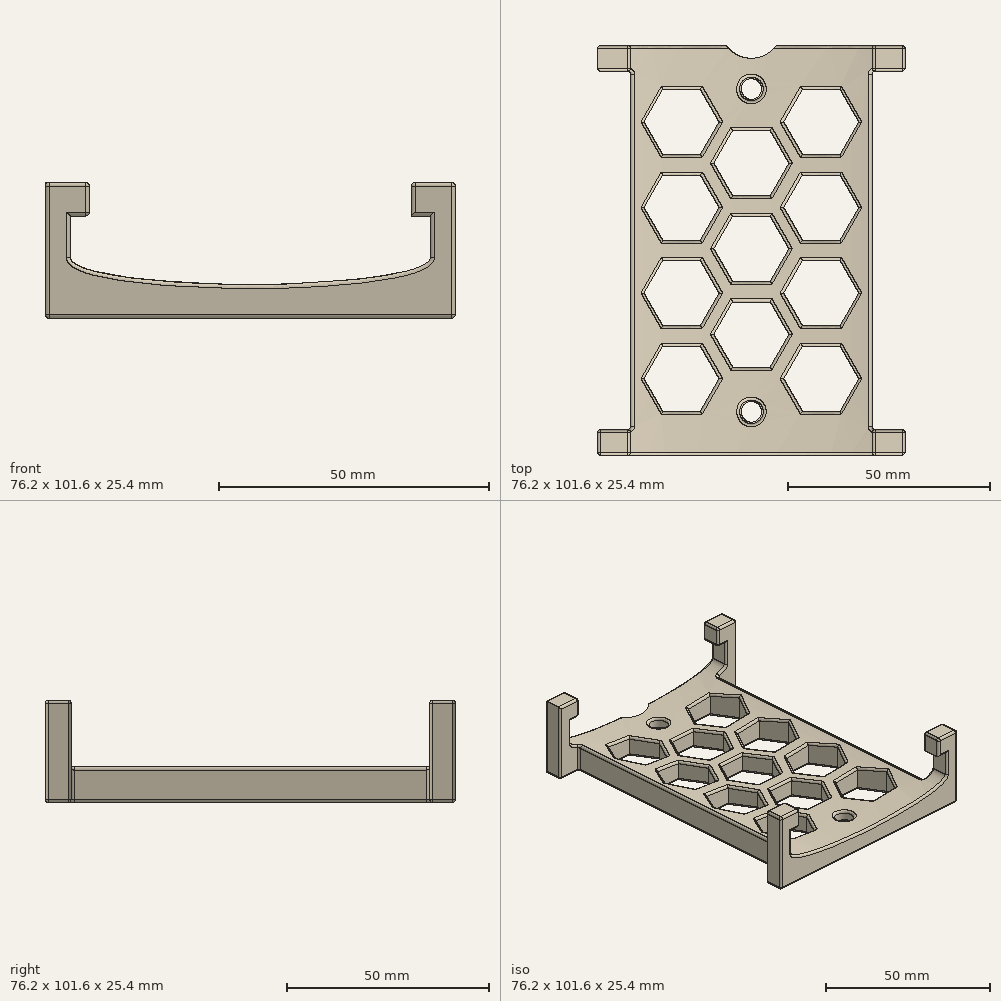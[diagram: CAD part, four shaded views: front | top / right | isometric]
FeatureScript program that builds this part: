
annotation { "Feature Type Name" : "Feature", "Feature Type Description" : "" }
export const myFeature = defineFeature(function(context is Context, id is Id, definition is map)
    precondition{}
    {
        {
            var Q0;
            Q0=qCreatedBy(makeId("Front.planeOp"),FACE);
            var sketch = newSketch(context, id + "F0", { "sketchPlane" : qUnion([Q0])});
            skLineSegment(sketch, "E0.bottom", {"start": v(-38.1, 25.4) * mm, "end": v(38.1, 25.4) * mm});
            skLineSegment(sketch, "E0.top", {"start": v(-38.1, 0) * mm, "end": v(38.1, 0) * mm});
            skLineSegment(sketch, "E0.left", {"start": v(-38.1, 25.4) * mm, "end": v(-38.1, 0) * mm});
            skLineSegment(sketch, "E0.right", {"start": v(38.1, 25.4) * mm, "end": v(38.1, 0) * mm});
            skLineSegment(sketch, "E1.top", {"start": v(33.46, 19.05) * mm, "end": v(-33.46, 19.05) * mm});
            skLineSegment(sketch, "E1.left", {"start": v(33.46, 11.43) * mm, "end": v(33.46, 19.05) * mm});
            skLineSegment(sketch, "E1.right", {"start": v(-33.46, 11.43) * mm, "end": v(-33.46, 19.05) * mm});
            skPoint(sketch, "E1.middle", {"position": v(0, 12.7) * mm});
            skPoint(sketch, "E1.middle.positionSnap0", {"position": v(-38.1, 12.7) * mm});
            skPoint(sketch, "E1.centerSnap0", {"position": v(-38.1, 12.7) * mm});
            skPoint(sketch, "E2", {"position": v(-33.46, 11.43) * mm});
            skPoint(sketch, "E3", {"position": v(33.46, 11.43) * mm});
            skFitSpline(sketch, "E4", {"points": [v(-33.46, 11.43) * mm, v(0, 6.35) * mm, v(33.46, 11.43) * mm, v(0, 19.05) * mm, v(-33.46, 11.43) * mm]});
            skPoint(sketch, "E5.orphan", {"position": v(33.46, 6.35) * mm});
            skPoint(sketch, "E6.orphan", {"position": v(-33.46, 6.35) * mm});
            skLineSegment(sketch, "E7", {"start": v(33.46, 11.47) * mm, "end": v(33.46, 6.35) * mm, "construction": true});
            skLineSegment(sketch, "E8", {"start": v(33.46, 6.35) * mm, "end": v(-33.46, 6.35) * mm, "construction": true});
            skLineSegment(sketch, "E9", {"start": v(-33.46, 11.47) * mm, "end": v(-33.46, 6.35) * mm, "construction": true});
            skLineSegment(sketch, "E10", {"start": v(29.93, 25.4) * mm, "end": v(29.93, 19.05) * mm});
            skLineSegment(sketch, "E11", {"start": v(-29.93, 19.05) * mm, "end": v(-29.93, 25.4) * mm});
            skLineSegment(sketch, "E12", {"start": v(-29.93, 19.05) * mm, "end": v(-38.1, 19.05) * mm, "construction": true});
            skLineSegment(sketch, "E13", {"start": v(29.93, 19.05) * mm, "end": v(38.1, 19.05) * mm, "construction": true});
            skSolve(sketch);
        }
        {
            var Q0;
            Q0=makeQuery(id+"F0.imprint","IMPRINT",FACE,{"disambiguationData":[TD([[makeQuery(id+"F0.imprint","IMPRINT",EDGE,{"derivedFrom":sQuery(id+"F0.wireOp",EDGE,"E0.top")}),1.0]])]});
            extrude(context, id + "F1", {"entities" : qUnion([Q0]), "depth" : 101.6 * mm});
        }
        {
            var Q0;
            {var subQ0=sQuery(id+"F0.wireOp",EDGE,"E0.bottom");Q0=makeQuery(id+"F1.opExtrude","SWEPT_FACE",FACE,{"disambiguationData":[OSD([subQ0]),TDD([makeQuery(id+"F0.imprint","IMPRINT",EDGE,{"disambiguationData":[TD([[makeQuery(id+"F0.imprint","INTERSECT",VERTEX,{"derivedFrom":[subQ0,sQuery(id+"F0.wireOp",EDGE,"E0.right")]}),1.0]])],"derivedFrom":subQ0})])]});}
            var sketch = newSketch(context, id + "F2", { "sketchPlane" : qUnion([Q0])});
            skLineSegment(sketch, "E14.bottom", {"start": v(29.93, -6.35) * mm, "end": v(38.1, -6.35) * mm});
            skLineSegment(sketch, "E14.top", {"start": v(29.93, -95.25) * mm, "end": v(38.1, -95.25) * mm});
            skLineSegment(sketch, "E14.left", {"start": v(29.93, -6.35) * mm, "end": v(29.93, -95.25) * mm});
            skLineSegment(sketch, "E14.right", {"start": v(38.1, -6.35) * mm, "end": v(38.1, -95.25) * mm});
            skLineSegment(sketch, "E15.bottom", {"start": v(-29.93, -6.35) * mm, "end": v(-38.1, -6.35) * mm});
            skLineSegment(sketch, "E15.top", {"start": v(-29.93, -95.25) * mm, "end": v(-38.1, -95.25) * mm});
            skLineSegment(sketch, "E15.left", {"start": v(-29.93, -6.35) * mm, "end": v(-29.93, -95.25) * mm});
            skLineSegment(sketch, "E15.right", {"start": v(-38.1, -6.35) * mm, "end": v(-38.1, -95.25) * mm});
            skSolve(sketch);
        }
        {
            var Q0;
            Q0=makeQuery(id+"F2.imprint","IMPRINT",FACE,{"disambiguationData":[TD([[makeQuery(id+"F2.imprint","IMPRINT",EDGE,{"derivedFrom":sQuery(id+"F2.wireOp",EDGE,"E15.bottom")}),1.0]])]});
            var Q1;
            Q1=makeQuery(id+"F2.imprint","IMPRINT",FACE,{"disambiguationData":[TD([[makeQuery(id+"F2.imprint","IMPRINT",EDGE,{"derivedFrom":sQuery(id+"F2.wireOp",EDGE,"E14.bottom")}),-1.0]])]});
            extrude(context, id + "F3", {"entities" : qUnion([Q0, Q1]), "operationType" : NewBodyOperationType.REMOVE, "endBound" : BoundingType.THROUGH_ALL, "oppositeDirection" : true, "depth" : 25.4 * mm});
        }
        {
            var Q0;
            Q0=makeQuery(id+"F1.opExtrude","SWEPT_FACE",FACE,{"disambiguationData":[OSD([sQuery(id+"F0.wireOp",EDGE,"E0.top")])]});
            var sketch = newSketch(context, id + "F4", { "sketchPlane" : qUnion([Q0])});
            skCircle(sketch, "E16", {"center": v(0, 90.8) * mm, "radius": 2.54 * mm});
            skCircle(sketch, "E17", {"center": v(0, 10.8) * mm, "radius": 2.54 * mm});
            skLineSegment(sketch, "E18", {"start": v(0, 90.8) * mm, "end": v(0, 101.6) * mm});
            skLineSegment(sketch, "E19", {"start": v(0, 10.8) * mm, "end": v(0, 0) * mm});
            skLineSegment(sketch, "E20", {"start": v(0, 10.8) * mm, "end": v(0, 90.8) * mm});
            skCircle(sketch, "E21", {"center": v(0, -4.44) * mm, "radius": 7.62 * mm});
            skSolve(sketch);
        }
        {
            var Q0;
            {var subQ0=sQuery(id+"F4.wireOp",EDGE,"E18");var subQ1=sQuery(id+"F4.wireOp",EDGE,"E16");var subQ2=makeQuery(id+"F4.imprint","INTERSECT",VERTEX,{"derivedFrom":[subQ1,subQ0]});Q0=makeQuery(id+"F4.imprint","IMPRINT",FACE,{"disambiguationData":[TD([[makeQuery(id+"F4.imprint","IMPRINT",EDGE,{"disambiguationData":[TD([[subQ2,-1.0]])],"derivedFrom":subQ1}),1.0]])]});}
            var Q1;
            {var subQ0=sQuery(id+"F4.wireOp",EDGE,"E18");var subQ1=sQuery(id+"F4.wireOp",EDGE,"E16");var subQ2=makeQuery(id+"F4.imprint","INTERSECT",VERTEX,{"derivedFrom":[subQ1,subQ0]});Q1=makeQuery(id+"F4.imprint","IMPRINT",FACE,{"disambiguationData":[TD([[makeQuery(id+"F4.imprint","IMPRINT",EDGE,{"disambiguationData":[TD([[subQ2,1.0]])],"derivedFrom":subQ1}),1.0]])]});}
            var Q2;
            {var subQ0=sQuery(id+"F4.wireOp",EDGE,"E19");var subQ1=sQuery(id+"F4.wireOp",EDGE,"E17");var subQ2=makeQuery(id+"F4.imprint","INTERSECT",VERTEX,{"derivedFrom":[subQ1,subQ0]});Q2=makeQuery(id+"F4.imprint","IMPRINT",FACE,{"disambiguationData":[TD([[makeQuery(id+"F4.imprint","IMPRINT",EDGE,{"disambiguationData":[TD([[subQ2,-1.0]])],"derivedFrom":subQ1}),1.0]])]});}
            var Q3;
            {var subQ0=sQuery(id+"F4.wireOp",EDGE,"E19");var subQ1=sQuery(id+"F4.wireOp",EDGE,"E17");var subQ2=makeQuery(id+"F4.imprint","INTERSECT",VERTEX,{"derivedFrom":[subQ1,subQ0]});Q3=makeQuery(id+"F4.imprint","IMPRINT",FACE,{"disambiguationData":[TD([[makeQuery(id+"F4.imprint","IMPRINT",EDGE,{"disambiguationData":[TD([[subQ2,1.0]])],"derivedFrom":subQ1}),1.0]])]});}
            extrude(context, id + "F5", {"entities" : qUnion([Q0, Q1, Q2, Q3]), "operationType" : NewBodyOperationType.REMOVE, "endBound" : BoundingType.THROUGH_ALL, "oppositeDirection" : true, "depth" : 25.4 * mm});
        }
        {
            var Q0;
            {var subQ1=sQuery(id+"F0.wireOp",EDGE,"E0.left");var subQ2=sQuery(id+"F0.wireOp",EDGE,"E0.bottom");Q0=makeQuery(id+"F3.boolean.opBoolean","SPLIT",FACE,{"disambiguationData":[TD([makeQuery(id+"F3.opExtrude","SWEPT_FACE",FACE,{"disambiguationData":[OSD([sQuery(id+"F2.wireOp",EDGE,"E15.top")])]})])],"derivedFrom":makeQuery(id+"F1.opExtrude","SWEPT_FACE",FACE,{"disambiguationData":[OSD([subQ2]),TDD([makeQuery(id+"F0.imprint","IMPRINT",EDGE,{"disambiguationData":[TD([[makeQuery(id+"F0.imprint","INTERSECT",VERTEX,{"derivedFrom":[subQ2,subQ1]}),-1.0]])],"derivedFrom":subQ2})])]})});}
            var sketch = newSketch(context, id + "F6", { "sketchPlane" : qUnion([Q0])});
            skCircle(sketch, "E22.0", {"center": v(0, -90.8) * mm, "radius": 2.92 * mm});
            skCircle(sketch, "E22.1", {"center": v(0, -10.8) * mm, "radius": 2.92 * mm});
            skSolve(sketch);
        }
        {
            var Q0;
            Q0=makeQuery(id+"F6.imprint","IMPRINT",FACE,{"disambiguationData":[TD([[makeQuery(id+"F6.imprint","IMPRINT",EDGE,{"derivedFrom":sQuery(id+"F6.wireOp",EDGE,"E22.1")}),1.0]])]});
            var Q1;
            Q1=makeQuery(id+"F6.imprint","IMPRINT",FACE,{"disambiguationData":[TD([[makeQuery(id+"F6.imprint","IMPRINT",EDGE,{"derivedFrom":sQuery(id+"F6.wireOp",EDGE,"E22.0")}),1.0]])]});
            extrude(context, id + "F7", {"entities" : qUnion([Q0, Q1]), "operationType" : NewBodyOperationType.REMOVE, "oppositeDirection" : true, "depth" : 22.1 * mm});
        }
        {
            var Q0;
            {var subQ1=sQuery(id+"F0.wireOp",EDGE,"E0.right");var subQ2=sQuery(id+"F0.wireOp",EDGE,"E0.bottom");Q0=makeQuery(id+"F3.boolean.opBoolean","SPLIT",FACE,{"disambiguationData":[TD([makeQuery(id+"F3.opExtrude","SWEPT_FACE",FACE,{"disambiguationData":[OSD([sQuery(id+"F2.wireOp",EDGE,"E14.bottom")])]})])],"derivedFrom":makeQuery(id+"F1.opExtrude","SWEPT_FACE",FACE,{"disambiguationData":[OSD([subQ2]),TDD([makeQuery(id+"F0.imprint","IMPRINT",EDGE,{"disambiguationData":[TD([[makeQuery(id+"F0.imprint","INTERSECT",VERTEX,{"derivedFrom":[subQ2,subQ1]}),1.0]])],"derivedFrom":subQ2})])]})});}
            var Q1;
            Q1=makeQuery(id+"F1.opExtrude","CAP_FACE",FACE,{"disambiguationData":[OSD([sQuery(id+"F0.wireOp",EDGE,"E0.bottom"),sQuery(id+"F0.wireOp",EDGE,"E0.top"),sQuery(id+"F0.wireOp",EDGE,"E0.left"),sQuery(id+"F0.wireOp",EDGE,"E0.right"),sQuery(id+"F0.wireOp",EDGE,"E1.top"),sQuery(id+"F0.wireOp",EDGE,"E1.left"),sQuery(id+"F0.wireOp",EDGE,"E1.right"),sQuery(id+"F0.wireOp",EDGE,"E4"),sQuery(id+"F0.wireOp",EDGE,"E10"),sQuery(id+"F0.wireOp",EDGE,"E11")])],"isStart":true});
            var Q2;
            {var subQ0=sQuery(id+"F0.wireOp",EDGE,"E10");Q2=makeQuery(id+"F3.boolean.opBoolean","SPLIT",FACE,{"disambiguationData":[TD([makeQuery(id+"F3.opExtrude","SWEPT_FACE",FACE,{"disambiguationData":[OSD([sQuery(id+"F2.wireOp",EDGE,"E14.bottom")])]})])],"derivedFrom":makeQuery(id+"F1.opExtrude","SWEPT_FACE",FACE,{"disambiguationData":[OSD([subQ0])]})});}
            var Q3;
            {var subQ1=sQuery(id+"F0.wireOp",EDGE,"E0.right");Q3=makeQuery(id+"F3.boolean.opBoolean","SPLIT",FACE,{"disambiguationData":[TD([makeQuery(id+"F3.opExtrude","SWEPT_FACE",FACE,{"disambiguationData":[OSD([sQuery(id+"F2.wireOp",EDGE,"E14.bottom")])]})])],"derivedFrom":makeQuery(id+"F1.opExtrude","SWEPT_FACE",FACE,{"disambiguationData":[OSD([subQ1])]})});}
            var Q4;
            Q4=makeQuery(id+"F3.boolean.opBoolean","COPY",FACE,{"derivedFrom":makeQuery(id+"F3.opExtrude","SWEPT_FACE",FACE,{"disambiguationData":[OSD([sQuery(id+"F2.wireOp",EDGE,"E14.bottom")])]})});
            var Q5;
            {var subQ1=sQuery(id+"F0.wireOp",EDGE,"E0.right");var subQ2=sQuery(id+"F0.wireOp",EDGE,"E0.bottom");Q5=makeQuery(id+"F3.boolean.opBoolean","SPLIT",FACE,{"disambiguationData":[TD([makeQuery(id+"F3.opExtrude","SWEPT_FACE",FACE,{"disambiguationData":[OSD([sQuery(id+"F2.wireOp",EDGE,"E14.top")])]})])],"derivedFrom":makeQuery(id+"F1.opExtrude","SWEPT_FACE",FACE,{"disambiguationData":[OSD([subQ2]),TDD([makeQuery(id+"F0.imprint","IMPRINT",EDGE,{"disambiguationData":[TD([[makeQuery(id+"F0.imprint","INTERSECT",VERTEX,{"derivedFrom":[subQ2,subQ1]}),1.0]])],"derivedFrom":subQ2})])]})});}
            var Q6;
            Q6=makeQuery(id+"F3.boolean.opBoolean","COPY",FACE,{"derivedFrom":makeQuery(id+"F3.opExtrude","SWEPT_FACE",FACE,{"disambiguationData":[OSD([sQuery(id+"F2.wireOp",EDGE,"E14.top")])]})});
            var Q7;
            {var subQ1=sQuery(id+"F0.wireOp",EDGE,"E0.right");Q7=makeQuery(id+"F3.boolean.opBoolean","SPLIT",FACE,{"disambiguationData":[TD([makeQuery(id+"F3.opExtrude","SWEPT_FACE",FACE,{"disambiguationData":[OSD([sQuery(id+"F2.wireOp",EDGE,"E14.top")])]})])],"derivedFrom":makeQuery(id+"F1.opExtrude","SWEPT_FACE",FACE,{"disambiguationData":[OSD([subQ1])]})});}
            var Q8;
            Q8=makeQuery(id+"F1.opExtrude","SWEPT_FACE",FACE,{"disambiguationData":[OSD([sQuery(id+"F0.wireOp",EDGE,"E0.top")])]});
            var Q9;
            {var subQ0=sQuery(id+"F0.wireOp",EDGE,"E0.left");Q9=makeQuery(id+"F3.boolean.opBoolean","SPLIT",FACE,{"disambiguationData":[TD([makeQuery(id+"F3.opExtrude","SWEPT_FACE",FACE,{"disambiguationData":[OSD([sQuery(id+"F2.wireOp",EDGE,"E15.top")])]})])],"derivedFrom":makeQuery(id+"F1.opExtrude","SWEPT_FACE",FACE,{"disambiguationData":[OSD([subQ0])]})});}
            var Q10;
            Q10=makeQuery(id+"F3.boolean.opBoolean","COPY",FACE,{"derivedFrom":makeQuery(id+"F3.opExtrude","SWEPT_FACE",FACE,{"disambiguationData":[OSD([sQuery(id+"F2.wireOp",EDGE,"E15.top")])]})});
            var Q11;
            Q11=makeQuery(id+"F3.boolean.opBoolean","COPY",FACE,{"derivedFrom":makeQuery(id+"F3.opExtrude","SWEPT_FACE",FACE,{"disambiguationData":[OSD([sQuery(id+"F2.wireOp",EDGE,"E15.bottom")])]})});
            var Q12;
            {var subQ2=sQuery(id+"F0.wireOp",EDGE,"E11");Q12=makeQuery(id+"F3.boolean.opBoolean","SPLIT",FACE,{"disambiguationData":[TD([makeQuery(id+"F3.opExtrude","SWEPT_FACE",FACE,{"disambiguationData":[OSD([sQuery(id+"F2.wireOp",EDGE,"E15.bottom")])]})])],"derivedFrom":makeQuery(id+"F1.opExtrude","SWEPT_FACE",FACE,{"disambiguationData":[OSD([subQ2])]})});}
            var Q13;
            Q13=makeQuery(id+"F1.opExtrude","CAP_FACE",FACE,{"disambiguationData":[OSD([sQuery(id+"F0.wireOp",EDGE,"E0.bottom"),sQuery(id+"F0.wireOp",EDGE,"E0.top"),sQuery(id+"F0.wireOp",EDGE,"E0.left"),sQuery(id+"F0.wireOp",EDGE,"E0.right"),sQuery(id+"F0.wireOp",EDGE,"E1.top"),sQuery(id+"F0.wireOp",EDGE,"E1.left"),sQuery(id+"F0.wireOp",EDGE,"E1.right"),sQuery(id+"F0.wireOp",EDGE,"E4"),sQuery(id+"F0.wireOp",EDGE,"E10"),sQuery(id+"F0.wireOp",EDGE,"E11")])],"isStart":false});
            var Q14;
            Q14=makeQuery(id+"F3.boolean.opBoolean","COPY",FACE,{"derivedFrom":makeQuery(id+"F3.opExtrude","SWEPT_FACE",FACE,{"disambiguationData":[OSD([sQuery(id+"F2.wireOp",EDGE,"E14.left")])]})});
            var Q15;
            {var subQ2=sQuery(id+"F0.wireOp",EDGE,"E11");Q15=makeQuery(id+"F3.boolean.opBoolean","SPLIT",FACE,{"disambiguationData":[TD([makeQuery(id+"F3.opExtrude","SWEPT_FACE",FACE,{"disambiguationData":[OSD([sQuery(id+"F2.wireOp",EDGE,"E15.top")])]})])],"derivedFrom":makeQuery(id+"F1.opExtrude","SWEPT_FACE",FACE,{"disambiguationData":[OSD([subQ2])]})});}
            var Q16;
            Q16=makeQuery(id+"F1.opExtrude","SWEPT_FACE",FACE,{"disambiguationData":[OSD([sQuery(id+"F0.wireOp",EDGE,"E4")])]});
            fillet(context, id + "F8", {"entities" : qUnion([Q0, Q1, Q2, Q3, Q4, Q5, Q6, Q7, Q8, Q9, Q10, Q11, Q12, Q13, Q14, Q15, Q16]), "radius" : 0.76 * mm, "tangentPropagation" : true, "allowEdgeOverflow" : false});
        }
        {
            var Q0;
            Q0=makeQuery(id+"F1.opExtrude","SWEPT_FACE",FACE,{"disambiguationData":[OSD([sQuery(id+"F0.wireOp",EDGE,"E0.top")])]});
            var sketch = newSketch(context, id + "F9", { "sketchPlane" : qUnion([Q0])});
            skCircle(sketch, "E23.cCircle", {"center": v(17.32, 82.61) * mm, "radius": 8.06 * mm, "construction": true});
            skLineSegment(sketch, "E23.0", {"start": v(26.63, 82.61) * mm, "end": v(21.98, 74.55) * mm});
            skLineSegment(sketch, "E23.1", {"start": v(21.98, 74.55) * mm, "end": v(12.66, 74.55) * mm});
            skLineSegment(sketch, "E23.2", {"start": v(12.66, 74.55) * mm, "end": v(8, 82.61) * mm});
            skLineSegment(sketch, "E23.3", {"start": v(8, 82.61) * mm, "end": v(12.66, 90.68) * mm});
            skLineSegment(sketch, "E23.4", {"start": v(12.66, 90.68) * mm, "end": v(21.98, 90.68) * mm});
            skLineSegment(sketch, "E23.5", {"start": v(21.98, 90.68) * mm, "end": v(26.63, 82.61) * mm});
            skPoint(sketch, "E23.0.midPoint", {"position": v(24.3, 78.58) * mm});
            skCircle(sketch, "E24.1.0.0", {"center": v(17.32, 61.4) * mm, "radius": 8.06 * mm, "construction": true});
            skPoint(sketch, "E24.1.0.1", {"position": v(24.3, 57.37) * mm});
            skLineSegment(sketch, "E24.1.0.2", {"start": v(26.63, 61.4) * mm, "end": v(21.98, 53.34) * mm});
            skLineSegment(sketch, "E24.1.0.3", {"start": v(21.98, 53.34) * mm, "end": v(12.66, 53.34) * mm});
            skLineSegment(sketch, "E24.1.0.4", {"start": v(12.66, 53.34) * mm, "end": v(8, 61.4) * mm});
            skLineSegment(sketch, "E24.1.0.5", {"start": v(8, 61.4) * mm, "end": v(12.66, 69.47) * mm});
            skLineSegment(sketch, "E24.1.0.6", {"start": v(12.66, 69.47) * mm, "end": v(21.98, 69.47) * mm});
            skLineSegment(sketch, "E24.1.0.7", {"start": v(21.98, 69.47) * mm, "end": v(26.63, 61.4) * mm});
            skCircle(sketch, "E24.2.0.0", {"center": v(17.32, 40.2) * mm, "radius": 8.06 * mm, "construction": true});
            skPoint(sketch, "E24.2.0.1", {"position": v(24.3, 36.16) * mm});
            skLineSegment(sketch, "E24.2.0.2", {"start": v(26.63, 40.2) * mm, "end": v(21.98, 32.13) * mm});
            skLineSegment(sketch, "E24.2.0.3", {"start": v(21.98, 32.13) * mm, "end": v(12.66, 32.13) * mm});
            skLineSegment(sketch, "E24.2.0.4", {"start": v(12.66, 32.13) * mm, "end": v(8, 40.2) * mm});
            skLineSegment(sketch, "E24.2.0.5", {"start": v(8, 40.2) * mm, "end": v(12.66, 48.26) * mm});
            skLineSegment(sketch, "E24.2.0.6", {"start": v(12.66, 48.26) * mm, "end": v(21.98, 48.26) * mm});
            skLineSegment(sketch, "E24.2.0.7", {"start": v(21.98, 48.26) * mm, "end": v(26.63, 40.2) * mm});
            skLineSegment(sketch, "E24.direction1", {"start": v(12.66, 74.55) * mm, "end": v(12.66, 53.34) * mm, "construction": true});
            skCircle(sketch, "E25.0.3.0", {"center": v(17.32, 18.99) * mm, "radius": 8.06 * mm, "construction": true});
            skPoint(sketch, "E25.2.3.0", {"position": v(24.3, 14.95) * mm});
            skLineSegment(sketch, "E25.3.3.0", {"start": v(26.63, 18.99) * mm, "end": v(21.98, 10.92) * mm});
            skLineSegment(sketch, "E25.6.3.0", {"start": v(21.98, 10.92) * mm, "end": v(12.66, 10.92) * mm});
            skLineSegment(sketch, "E25.9.3.0", {"start": v(12.66, 10.92) * mm, "end": v(8, 18.99) * mm});
            skLineSegment(sketch, "E25.12.3.0", {"start": v(8, 18.99) * mm, "end": v(12.66, 27.05) * mm});
            skLineSegment(sketch, "E25.15.3.0", {"start": v(12.66, 27.05) * mm, "end": v(21.98, 27.05) * mm});
            skLineSegment(sketch, "E25.18.3.0", {"start": v(21.98, 27.05) * mm, "end": v(26.63, 18.99) * mm});
            skLineSegment(sketch, "E26", {"start": v(0, 0) * mm, "end": v(0, 100.84) * mm, "construction": true});
            skLineSegment(sketch, "E27.MirrorCS", {"start": v(-8, 18.99) * mm, "end": v(-12.66, 27.05) * mm});
            skLineSegment(sketch, "E28.MirrorCS", {"start": v(-21.98, 69.47) * mm, "end": v(-26.63, 61.4) * mm});
            skLineSegment(sketch, "E29.MirrorCS", {"start": v(-21.98, 32.13) * mm, "end": v(-12.66, 32.13) * mm});
            skLineSegment(sketch, "E30.MirrorCS", {"start": v(-21.98, 48.26) * mm, "end": v(-26.63, 40.2) * mm});
            skLineSegment(sketch, "E31.MirrorCS", {"start": v(-26.63, 82.61) * mm, "end": v(-21.98, 74.55) * mm});
            skLineSegment(sketch, "E32.MirrorCS", {"start": v(-21.98, 74.55) * mm, "end": v(-12.66, 74.55) * mm});
            skLineSegment(sketch, "E33.MirrorCS", {"start": v(-8, 82.61) * mm, "end": v(-12.66, 90.68) * mm});
            skLineSegment(sketch, "E34.MirrorCS", {"start": v(-21.98, 90.68) * mm, "end": v(-26.63, 82.61) * mm});
            skLineSegment(sketch, "E35.MirrorCS", {"start": v(-26.63, 61.4) * mm, "end": v(-21.98, 53.34) * mm});
            skLineSegment(sketch, "E36.MirrorCS", {"start": v(-21.98, 27.05) * mm, "end": v(-26.63, 18.99) * mm});
            skLineSegment(sketch, "E37.MirrorCS", {"start": v(-26.63, 40.2) * mm, "end": v(-21.98, 32.13) * mm});
            skLineSegment(sketch, "E38.MirrorCS", {"start": v(-12.66, 27.05) * mm, "end": v(-21.98, 27.05) * mm});
            skLineSegment(sketch, "E39.MirrorCS", {"start": v(-21.98, 10.92) * mm, "end": v(-12.66, 10.92) * mm});
            skLineSegment(sketch, "E40.MirrorCS", {"start": v(-21.98, 53.34) * mm, "end": v(-12.66, 53.34) * mm});
            skLineSegment(sketch, "E41.MirrorCS", {"start": v(-12.66, 53.34) * mm, "end": v(-8, 61.4) * mm});
            skLineSegment(sketch, "E42.MirrorCS", {"start": v(-8, 61.4) * mm, "end": v(-12.66, 69.47) * mm});
            skLineSegment(sketch, "E43.MirrorCS", {"start": v(-12.66, 69.47) * mm, "end": v(-21.98, 69.47) * mm});
            skLineSegment(sketch, "E44.MirrorCS", {"start": v(-12.66, 10.92) * mm, "end": v(-8, 18.99) * mm});
            skLineSegment(sketch, "E45.MirrorCS", {"start": v(-26.63, 18.99) * mm, "end": v(-21.98, 10.92) * mm});
            skLineSegment(sketch, "E46.MirrorCS", {"start": v(-8, 40.2) * mm, "end": v(-12.66, 48.26) * mm});
            skLineSegment(sketch, "E47.MirrorCS", {"start": v(-12.66, 32.13) * mm, "end": v(-8, 40.2) * mm});
            skLineSegment(sketch, "E48.MirrorCS", {"start": v(-12.66, 48.26) * mm, "end": v(-21.98, 48.26) * mm});
            skPoint(sketch, "E49.MirrorP", {"position": v(-24.3, 36.16) * mm});
            skPoint(sketch, "E50.MirrorP", {"position": v(-24.3, 78.58) * mm});
            skLineSegment(sketch, "E51.MirrorCS", {"start": v(-12.66, 90.68) * mm, "end": v(-21.98, 90.68) * mm});
            skCircle(sketch, "E52.MirrorC", {"center": v(-17.32, 61.4) * mm, "radius": 8.06 * mm, "construction": true});
            skCircle(sketch, "E53.MirrorC", {"center": v(-17.32, 18.99) * mm, "radius": 8.06 * mm, "construction": true});
            skLineSegment(sketch, "E54.MirrorCS", {"start": v(-12.66, 74.55) * mm, "end": v(-12.66, 53.34) * mm, "construction": true});
            skPoint(sketch, "E55.MirrorP", {"position": v(-24.3, 57.37) * mm});
            skCircle(sketch, "E56.MirrorC", {"center": v(-17.32, 40.2) * mm, "radius": 8.06 * mm, "construction": true});
            skCircle(sketch, "E57.MirrorC", {"center": v(-17.32, 82.61) * mm, "radius": 8.06 * mm, "construction": true});
            skLineSegment(sketch, "E58.MirrorCS", {"start": v(-12.66, 74.55) * mm, "end": v(-8, 82.61) * mm});
            skPoint(sketch, "E59.MirrorP", {"position": v(-24.3, 14.95) * mm});
            skCircle(sketch, "E60.cCircle", {"center": v(0, 71.63) * mm, "radius": 8.06 * mm, "construction": true});
            skLineSegment(sketch, "E60.0", {"start": v(9.31, 71.63) * mm, "end": v(4.66, 63.56) * mm});
            skLineSegment(sketch, "E60.1", {"start": v(4.66, 63.56) * mm, "end": v(-4.66, 63.56) * mm});
            skLineSegment(sketch, "E60.2", {"start": v(-4.66, 63.56) * mm, "end": v(-9.31, 71.63) * mm});
            skLineSegment(sketch, "E60.3", {"start": v(-9.31, 71.63) * mm, "end": v(-4.66, 79.7) * mm});
            skLineSegment(sketch, "E60.4", {"start": v(-4.66, 79.7) * mm, "end": v(4.66, 79.7) * mm});
            skLineSegment(sketch, "E60.5", {"start": v(4.66, 79.7) * mm, "end": v(9.31, 71.63) * mm});
            skPoint(sketch, "E60.0.midPoint", {"position": v(6.98, 67.6) * mm});
            skCircle(sketch, "E61.1.0.0", {"center": v(0, 50.42) * mm, "radius": 8.06 * mm, "construction": true});
            skPoint(sketch, "E61.1.0.1", {"position": v(6.98, 46.39) * mm});
            skLineSegment(sketch, "E61.1.0.2", {"start": v(9.31, 50.42) * mm, "end": v(4.66, 42.35) * mm});
            skLineSegment(sketch, "E61.1.0.3", {"start": v(4.66, 42.35) * mm, "end": v(-4.66, 42.35) * mm});
            skLineSegment(sketch, "E61.1.0.4", {"start": v(-4.66, 42.35) * mm, "end": v(-9.31, 50.42) * mm});
            skLineSegment(sketch, "E61.1.0.5", {"start": v(-9.31, 50.42) * mm, "end": v(-4.66, 58.48) * mm});
            skLineSegment(sketch, "E61.1.0.6", {"start": v(-4.66, 58.48) * mm, "end": v(4.66, 58.48) * mm});
            skLineSegment(sketch, "E61.1.0.7", {"start": v(4.66, 58.48) * mm, "end": v(9.31, 50.42) * mm});
            skCircle(sketch, "E61.2.0.0", {"center": v(0, 29.2) * mm, "radius": 8.06 * mm, "construction": true});
            skPoint(sketch, "E61.2.0.1", {"position": v(6.98, 25.18) * mm});
            skLineSegment(sketch, "E61.2.0.2", {"start": v(9.31, 29.21) * mm, "end": v(4.66, 21.15) * mm});
            skLineSegment(sketch, "E61.2.0.3", {"start": v(4.66, 21.15) * mm, "end": v(-4.66, 21.15) * mm});
            skLineSegment(sketch, "E61.2.0.4", {"start": v(-4.66, 21.15) * mm, "end": v(-9.31, 29.2) * mm});
            skLineSegment(sketch, "E61.2.0.5", {"start": v(-9.31, 29.2) * mm, "end": v(-4.66, 37.27) * mm});
            skLineSegment(sketch, "E61.2.0.6", {"start": v(-4.66, 37.27) * mm, "end": v(4.66, 37.27) * mm});
            skLineSegment(sketch, "E61.2.0.7", {"start": v(4.66, 37.27) * mm, "end": v(9.31, 29.21) * mm});
            skLineSegment(sketch, "E61.direction1", {"start": v(-4.66, 63.56) * mm, "end": v(-4.66, 42.35) * mm, "construction": true});
            skSolve(sketch);
        }
        {
            var Q0;
            Q0=qSketchRegion(id+"F9",true);
            var Q1;
            Q1=qConstructionFilter(qBodyType(qCreatedBy(id+"F9",EDGE),BodyType.WIRE),ConstructionObject.NO);
            extrude(context, id + "F10", {"entities" : qUnion([Q0]), "operationType" : NewBodyOperationType.REMOVE, "surfaceEntities" : qUnion([Q1]), "endBound" : BoundingType.THROUGH_ALL, "oppositeDirection" : true, "depth" : 25.4 * mm});
        }
        {
            var Q0;
            Q0=makeQuery(id+"F1.opExtrude","SWEPT_FACE",FACE,{"disambiguationData":[OSD([sQuery(id+"F0.wireOp",EDGE,"E4")])]});
            var Q1;
            Q1=makeQuery(id+"F1.opExtrude","SWEPT_FACE",FACE,{"disambiguationData":[OSD([sQuery(id+"F0.wireOp",EDGE,"E0.top")])]});
            fillet(context, id + "F11", {"entities" : qUnion([Q0, Q1]), "radius" : 0.76 * mm, "tangentPropagation" : true, "allowEdgeOverflow" : false});
        }
        {
            var Q0;
            {var subQ0=sQuery(id+"F4.wireOp",EDGE,"E19");var subQ1=makeQuery(id+"F1.opExtrude","CAP_EDGE",EDGE,{"disambiguationData":[OSD([sQuery(id+"F0.wireOp",EDGE,"E0.top")])],"isStart":true});var subQ2=makeQuery(id+"F4.imprint","INTERSECT",VERTEX,{"derivedFrom":[subQ1,subQ0]});Q0=makeQuery(id+"F4.imprint","IMPRINT",FACE,{"disambiguationData":[TD([[makeQuery(id+"F4.imprint","IMPRINT",EDGE,{"disambiguationData":[TD([[subQ2,1.0]])],"derivedFrom":subQ0}),1.0]])]});}
            var Q1;
            {var subQ0=sQuery(id+"F4.wireOp",EDGE,"E19");var subQ1=makeQuery(id+"F1.opExtrude","CAP_EDGE",EDGE,{"disambiguationData":[OSD([sQuery(id+"F0.wireOp",EDGE,"E0.top")])],"isStart":true});var subQ2=makeQuery(id+"F4.imprint","INTERSECT",VERTEX,{"derivedFrom":[subQ1,subQ0]});Q1=makeQuery(id+"F4.imprint","IMPRINT",FACE,{"disambiguationData":[TD([[makeQuery(id+"F4.imprint","IMPRINT",EDGE,{"disambiguationData":[TD([[subQ2,1.0]])],"derivedFrom":subQ0}),-1.0]])]});}
            extrude(context, id + "F12", {"entities" : qUnion([Q0, Q1]), "operationType" : NewBodyOperationType.REMOVE, "oppositeDirection" : true, "depth" : 25.4 * mm});
        }
    });
